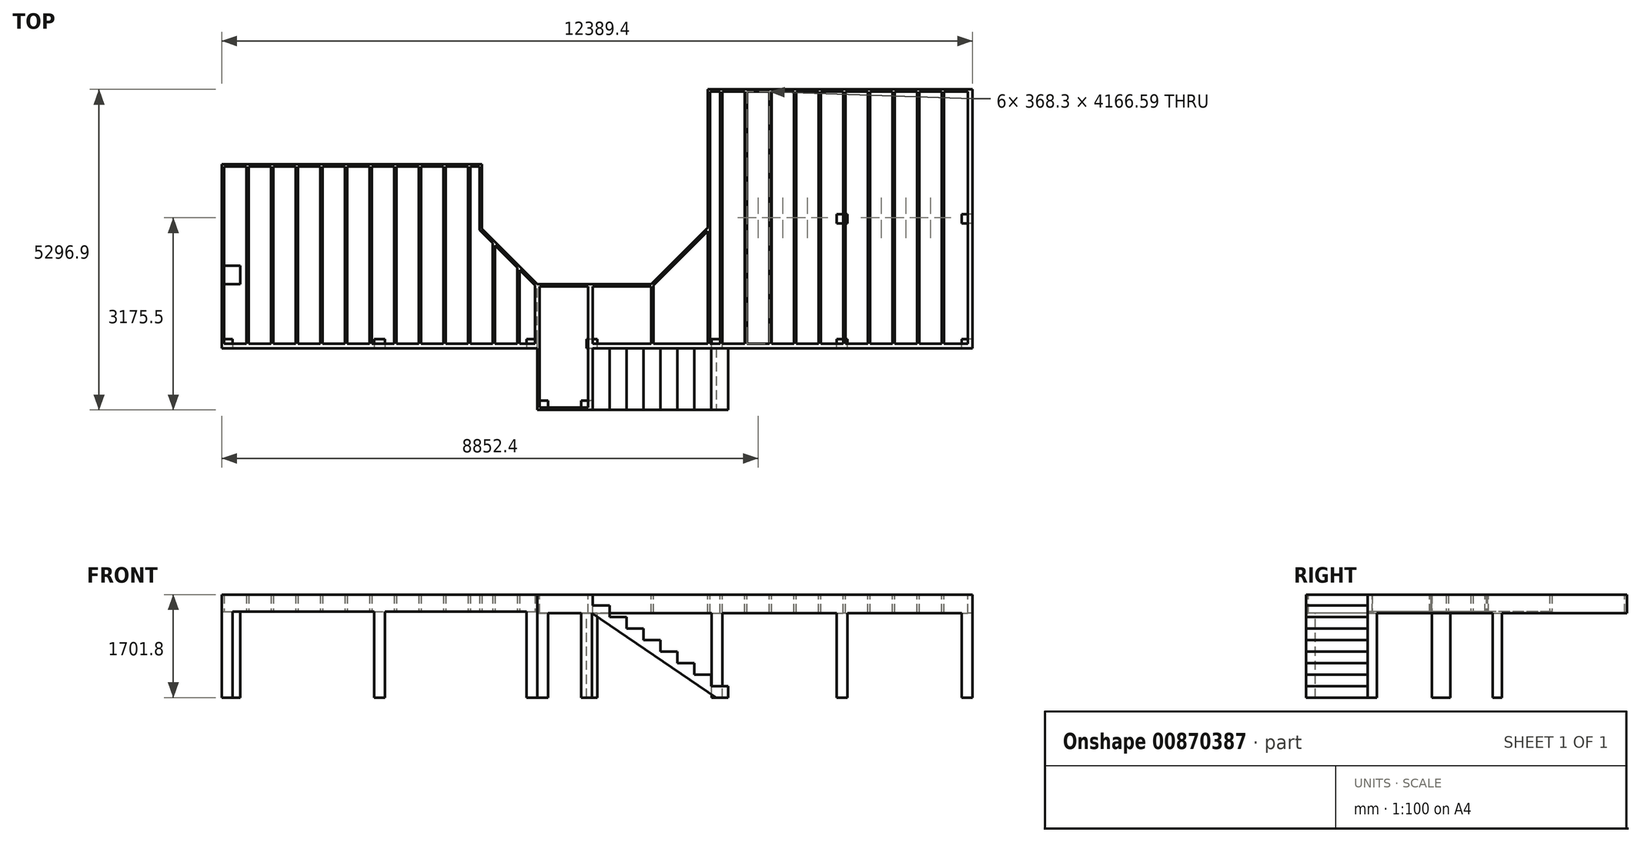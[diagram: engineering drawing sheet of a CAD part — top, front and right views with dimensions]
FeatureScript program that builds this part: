
annotation { "Feature Type Name" : "Feature", "Feature Type Description" : "" }
export const myFeature = defineFeature(function(context is Context, id is Id, definition is map)
    precondition{}
    {
        {
            var Q0;
            Q0=qCreatedBy(makeId("Top.planeOp"),FACE);
            var sketch = newSketch(context, id + "F0", { "sketchPlane" : qUnion([Q0])});
            skLineSegment(sketch, "E0.bottom", {"start": v(0, -1676.4) * mm, "end": v(304.8, -1676.4) * mm});
            skLineSegment(sketch, "E0.top", {"start": v(0, -1981.2) * mm, "end": v(304.8, -1981.2) * mm});
            skLineSegment(sketch, "E0.left", {"start": v(0, -1676.4) * mm, "end": v(0, -1981.2) * mm});
            skLineSegment(sketch, "E0.right", {"start": v(304.8, -1676.4) * mm, "end": v(304.8, -1981.2) * mm});
            skLineSegment(sketch, "E1.bottom", {"start": v(0, -2889.75) * mm, "end": v(177.8, -2889.75) * mm});
            skLineSegment(sketch, "E1.top", {"start": v(0, -3042.15) * mm, "end": v(177.8, -3042.15) * mm});
            skLineSegment(sketch, "E1.left", {"start": v(0, -2889.75) * mm, "end": v(0, -3042.15) * mm});
            skLineSegment(sketch, "E1.right", {"start": v(177.8, -2889.75) * mm, "end": v(177.8, -3042.15) * mm});
            skLineSegment(sketch, "E2.bottom", {"start": v(2514.6, -2889.75) * mm, "end": v(2692.4, -2889.75) * mm});
            skLineSegment(sketch, "E2.top", {"start": v(2514.6, -3042.15) * mm, "end": v(2692.4, -3042.15) * mm});
            skLineSegment(sketch, "E2.left", {"start": v(2514.6, -2889.75) * mm, "end": v(2514.6, -3042.15) * mm});
            skLineSegment(sketch, "E2.right", {"start": v(2692.4, -2889.75) * mm, "end": v(2692.4, -3042.15) * mm});
            skLineSegment(sketch, "E3.bottom", {"start": v(5029.2, -2889.75) * mm, "end": v(5207, -2889.75) * mm});
            skLineSegment(sketch, "E3.top", {"start": v(5029.2, -3042.15) * mm, "end": v(5207, -3042.15) * mm});
            skLineSegment(sketch, "E3.left", {"start": v(5029.2, -2889.75) * mm, "end": v(5029.2, -3042.15) * mm});
            skLineSegment(sketch, "E3.right", {"start": v(5207, -2889.75) * mm, "end": v(5207, -3042.15) * mm});
            skLineSegment(sketch, "E4", {"start": v(0, 0) * mm, "end": v(4292.6, 0) * mm, "construction": true});
            skLineSegment(sketch, "E5", {"start": v(4292.6, 0) * mm, "end": v(4292.6, -1066.8) * mm, "construction": true});
            skLineSegment(sketch, "E6", {"start": v(4292.6, -1066.8) * mm, "end": v(5226.55, -2000.75) * mm, "construction": true});
            skLineSegment(sketch, "E7", {"start": v(5226.55, -2000.75) * mm, "end": v(7106.15, -2000.75) * mm, "construction": true});
            skSolve(sketch);
        }
        {
            var Q0;
            Q0=qSketchRegion(id+"F0",true);
            extrude(context, id + "F1", {"entities" : qUnion([Q0]), "depth" : 1422.4 * mm, "offsetDistance" : 25.4 * mm});
        }
        {
            var Q0;
            Q0=makeQuery(id+"F1.opExtrude","CAP_FACE",FACE,{"disambiguationData":[OSD([sQuery(id+"F0.wireOp",EDGE,"E0.bottom"),sQuery(id+"F0.wireOp",EDGE,"E0.top"),sQuery(id+"F0.wireOp",EDGE,"E0.left"),sQuery(id+"F0.wireOp",EDGE,"E0.right")])],"isStart":false});
            var sketch = newSketch(context, id + "F2", { "sketchPlane" : qUnion([Q0])});
            skLineSegment(sketch, "E8.0", {"start": v(0, 0) * mm, "end": v(4292.6, 0) * mm});
            skLineSegment(sketch, "E9.0", {"start": v(4292.6, 0) * mm, "end": v(4292.6, -1066.8) * mm});
            skLineSegment(sketch, "E9.1", {"start": v(4292.6, -1066.8) * mm, "end": v(5207, -1981.2) * mm});
            skLineSegment(sketch, "E10", {"start": v(0, 0) * mm, "end": v(0, -3042.15) * mm});
            skLineSegment(sketch, "E11", {"start": v(0, -3042.15) * mm, "end": v(5207, -3042.15) * mm});
            skLineSegment(sketch, "E12", {"start": v(5207, -3042.15) * mm, "end": v(5207, -1981.2) * mm});
            skPoint(sketch, "E13.orphan", {"position": v(5226.55, -2000.75) * mm});
            skLineSegment(sketch, "E14.0", {"start": v(4254.5, -38.1) * mm, "end": v(4254.5, -1082.58) * mm});
            skLineSegment(sketch, "E14.1", {"start": v(5168.9, -3004.05) * mm, "end": v(5168.9, -1996.98) * mm});
            skLineSegment(sketch, "E14.2", {"start": v(38.1, -3004.05) * mm, "end": v(5168.9, -3004.05) * mm});
            skLineSegment(sketch, "E14.3", {"start": v(4254.5, -1082.58) * mm, "end": v(5168.9, -1996.98) * mm});
            skLineSegment(sketch, "E14.4", {"start": v(38.1, -38.1) * mm, "end": v(38.1, -3004.05) * mm});
            skLineSegment(sketch, "E14.5", {"start": v(38.1, -38.1) * mm, "end": v(4254.5, -38.1) * mm});
            skSolve(sketch);
        }
        {
            var Q0;
            Q0=qSketchRegion(id+"F2",true);
            extrude(context, id + "F3", {"entities" : qUnion([Q0]), "operationType" : NewBodyOperationType.ADD, "depth" : 279.4 * mm, "offsetDistance" : 25.4 * mm});
        }
        {
            var Q0;
            Q0=makeQuery(id+"F1.opExtrude","CAP_FACE",FACE,{"disambiguationData":[OSD([sQuery(id+"F0.wireOp",EDGE,"E1.bottom"),sQuery(id+"F0.wireOp",EDGE,"E1.top"),sQuery(id+"F0.wireOp",EDGE,"E1.left"),sQuery(id+"F0.wireOp",EDGE,"E1.right")])],"isStart":false});
            var sketch = newSketch(context, id + "F4", { "sketchPlane" : qUnion([Q0])});
            skPoint(sketch, "E15.oppositeSnap0", {"position": v(38.1, -2965.95) * mm});
            skLineSegment(sketch, "E15.bottom", {"start": v(38.1, -3004.05) * mm, "end": v(5168.9, -3004.05) * mm});
            skLineSegment(sketch, "E15.top", {"start": v(38.1, -2965.95) * mm, "end": v(5168.9, -2965.95) * mm});
            skLineSegment(sketch, "E15.left", {"start": v(38.1, -3004.05) * mm, "end": v(38.1, -2965.95) * mm});
            skLineSegment(sketch, "E15.right", {"start": v(5168.9, -3004.05) * mm, "end": v(5168.9, -2965.95) * mm});
            skSolve(sketch);
        }
        {
            var Q0;
            Q0=qSketchRegion(id+"F4",true);
            var Q1;
            Q1=makeQuery(id+"F3.opExtrude","CAP_FACE",FACE,{"disambiguationData":[OSD([sQuery(id+"F2.wireOp",EDGE,"E8.0"),sQuery(id+"F2.wireOp",EDGE,"E9.0"),sQuery(id+"F2.wireOp",EDGE,"E9.1"),sQuery(id+"F2.wireOp",EDGE,"E10"),sQuery(id+"F2.wireOp",EDGE,"E11"),sQuery(id+"F2.wireOp",EDGE,"E12"),sQuery(id+"F2.wireOp",EDGE,"E14.0"),sQuery(id+"F2.wireOp",EDGE,"E14.1"),sQuery(id+"F2.wireOp",EDGE,"E14.2"),sQuery(id+"F2.wireOp",EDGE,"E14.3"),sQuery(id+"F2.wireOp",EDGE,"E14.4"),sQuery(id+"F2.wireOp",EDGE,"E14.5")])],"isStart":false});
            extrude(context, id + "F5", {"entities" : qUnion([Q0]), "operationType" : NewBodyOperationType.ADD, "endBound" : BoundingType.UP_TO_SURFACE, "depth" : 25.4 * mm, "endBoundEntityFace" : qUnion([Q1]), "offsetDistance" : 25.4 * mm});
        }
        {
            var Q0;
            Q0=makeQuery(id+"F1.opExtrude","CAP_FACE",FACE,{"disambiguationData":[OSD([sQuery(id+"F0.wireOp",EDGE,"E0.bottom"),sQuery(id+"F0.wireOp",EDGE,"E0.top"),sQuery(id+"F0.wireOp",EDGE,"E0.left"),sQuery(id+"F0.wireOp",EDGE,"E0.right")])],"isStart":false});
            var sketch = newSketch(context, id + "F6", { "sketchPlane" : qUnion([Q0])});
            skLineSegment(sketch, "E16.bottom", {"start": v(406.4, -38.1) * mm, "end": v(444.5, -38.1) * mm});
            skLineSegment(sketch, "E16.top", {"start": v(406.4, -2965.95) * mm, "end": v(444.5, -2965.95) * mm});
            skLineSegment(sketch, "E16.left", {"start": v(406.4, -38.1) * mm, "end": v(406.4, -2965.95) * mm});
            skLineSegment(sketch, "E16.right", {"start": v(444.5, -38.1) * mm, "end": v(444.5, -2965.95) * mm});
            skLineSegment(sketch, "E17.1.0.0", {"start": v(850.9, -38.1) * mm, "end": v(850.9, -2965.95) * mm});
            skLineSegment(sketch, "E17.1.0.1", {"start": v(812.8, -38.1) * mm, "end": v(812.8, -2965.95) * mm});
            skLineSegment(sketch, "E17.1.0.2", {"start": v(812.8, -38.1) * mm, "end": v(850.9, -38.1) * mm});
            skLineSegment(sketch, "E17.1.0.3", {"start": v(812.8, -2965.95) * mm, "end": v(850.9, -2965.95) * mm});
            skLineSegment(sketch, "E17.2.0.0", {"start": v(1257.3, -38.1) * mm, "end": v(1257.3, -2965.95) * mm});
            skLineSegment(sketch, "E17.2.0.1", {"start": v(1219.2, -38.1) * mm, "end": v(1219.2, -2965.95) * mm});
            skLineSegment(sketch, "E17.2.0.2", {"start": v(1219.2, -38.1) * mm, "end": v(1257.3, -38.1) * mm});
            skLineSegment(sketch, "E17.2.0.3", {"start": v(1219.2, -2965.95) * mm, "end": v(1257.3, -2965.95) * mm});
            skLineSegment(sketch, "E17.3.0.0", {"start": v(1663.7, -38.1) * mm, "end": v(1663.7, -2965.95) * mm});
            skLineSegment(sketch, "E17.3.0.1", {"start": v(1625.6, -38.1) * mm, "end": v(1625.6, -2965.95) * mm});
            skLineSegment(sketch, "E17.3.0.2", {"start": v(1625.6, -38.1) * mm, "end": v(1663.7, -38.1) * mm});
            skLineSegment(sketch, "E17.3.0.3", {"start": v(1625.6, -2965.95) * mm, "end": v(1663.7, -2965.95) * mm});
            skLineSegment(sketch, "E17.4.0.0", {"start": v(2070.1, -38.1) * mm, "end": v(2070.1, -2965.95) * mm});
            skLineSegment(sketch, "E17.4.0.1", {"start": v(2032, -38.1) * mm, "end": v(2032, -2965.95) * mm});
            skLineSegment(sketch, "E17.4.0.2", {"start": v(2032, -38.1) * mm, "end": v(2070.1, -38.1) * mm});
            skLineSegment(sketch, "E17.4.0.3", {"start": v(2032, -2965.95) * mm, "end": v(2070.1, -2965.95) * mm});
            skLineSegment(sketch, "E17.5.0.0", {"start": v(2476.5, -38.1) * mm, "end": v(2476.5, -2965.95) * mm});
            skLineSegment(sketch, "E17.5.0.1", {"start": v(2438.4, -38.1) * mm, "end": v(2438.4, -2965.95) * mm});
            skLineSegment(sketch, "E17.5.0.2", {"start": v(2438.4, -38.1) * mm, "end": v(2476.5, -38.1) * mm});
            skLineSegment(sketch, "E17.5.0.3", {"start": v(2438.4, -2965.95) * mm, "end": v(2476.5, -2965.95) * mm});
            skLineSegment(sketch, "E17.6.0.0", {"start": v(2882.9, -38.1) * mm, "end": v(2882.9, -2965.95) * mm});
            skLineSegment(sketch, "E17.6.0.1", {"start": v(2844.8, -38.1) * mm, "end": v(2844.8, -2965.95) * mm});
            skLineSegment(sketch, "E17.6.0.2", {"start": v(2844.8, -38.1) * mm, "end": v(2882.9, -38.1) * mm});
            skLineSegment(sketch, "E17.6.0.3", {"start": v(2844.8, -2965.95) * mm, "end": v(2882.9, -2965.95) * mm});
            skLineSegment(sketch, "E17.7.0.0", {"start": v(3289.3, -38.1) * mm, "end": v(3289.3, -2965.95) * mm});
            skLineSegment(sketch, "E17.7.0.1", {"start": v(3251.2, -38.1) * mm, "end": v(3251.2, -2965.95) * mm});
            skLineSegment(sketch, "E17.7.0.2", {"start": v(3251.2, -38.1) * mm, "end": v(3289.3, -38.1) * mm});
            skLineSegment(sketch, "E17.7.0.3", {"start": v(3251.2, -2965.95) * mm, "end": v(3289.3, -2965.95) * mm});
            skLineSegment(sketch, "E17.8.0.0", {"start": v(3695.7, -38.1) * mm, "end": v(3695.7, -2965.95) * mm});
            skLineSegment(sketch, "E17.8.0.1", {"start": v(3657.6, -38.1) * mm, "end": v(3657.6, -2965.95) * mm});
            skLineSegment(sketch, "E17.8.0.2", {"start": v(3657.6, -38.1) * mm, "end": v(3695.7, -38.1) * mm});
            skLineSegment(sketch, "E17.8.0.3", {"start": v(3657.6, -2965.95) * mm, "end": v(3695.7, -2965.95) * mm});
            skLineSegment(sketch, "E17.9.0.0", {"start": v(4102.1, -38.1) * mm, "end": v(4102.1, -2965.95) * mm});
            skLineSegment(sketch, "E17.9.0.1", {"start": v(4064, -38.1) * mm, "end": v(4064, -2965.95) * mm});
            skLineSegment(sketch, "E17.9.0.2", {"start": v(4064, -38.1) * mm, "end": v(4102.1, -38.1) * mm});
            skLineSegment(sketch, "E17.9.0.3", {"start": v(4064, -2965.95) * mm, "end": v(4102.1, -2965.95) * mm});
            skLineSegment(sketch, "E17.direction1", {"start": v(406.4, -2965.95) * mm, "end": v(812.8, -2965.95) * mm, "construction": true});
            skLineSegment(sketch, "E18.top", {"start": v(4470.4, -2965.95) * mm, "end": v(4508.5, -2965.95) * mm});
            skLineSegment(sketch, "E18.left", {"start": v(4470.4, -1298.48) * mm, "end": v(4470.4, -2965.95) * mm});
            skLineSegment(sketch, "E18.right", {"start": v(4508.5, -1336.58) * mm, "end": v(4508.5, -2965.95) * mm});
            skLineSegment(sketch, "E19.top", {"start": v(4876.8, -2965.95) * mm, "end": v(4914.9, -2965.95) * mm});
            skLineSegment(sketch, "E19.left", {"start": v(4876.8, -1704.88) * mm, "end": v(4876.8, -2965.95) * mm});
            skLineSegment(sketch, "E19.right", {"start": v(4914.9, -1742.98) * mm, "end": v(4914.9, -2965.95) * mm});
            skLineSegment(sketch, "E20", {"start": v(4470.4, -1298.48) * mm, "end": v(4508.5, -1336.58) * mm});
            skLineSegment(sketch, "E21.trimOffspring", {"start": v(4876.8, -1704.88) * mm, "end": v(4914.9, -1742.98) * mm});
            skSolve(sketch);
        }
        {
            var Q0;
            Q0=qSketchRegion(id+"F6",true);
            var Q1;
            {var subQ0=sQuery(id+"F2.wireOp",EDGE,"E14.5");var subQ1=sQuery(id+"F2.wireOp",EDGE,"E14.4");var subQ2=sQuery(id+"F2.wireOp",EDGE,"E14.3");var subQ3=sQuery(id+"F2.wireOp",EDGE,"E14.2");var subQ4=sQuery(id+"F2.wireOp",EDGE,"E14.1");var subQ5=sQuery(id+"F2.wireOp",EDGE,"E14.0");var subQ6=sQuery(id+"F2.wireOp",EDGE,"E12");var subQ7=sQuery(id+"F2.wireOp",EDGE,"E11");var subQ8=sQuery(id+"F2.wireOp",EDGE,"E10");var subQ9=sQuery(id+"F2.wireOp",EDGE,"E9.1");var subQ10=sQuery(id+"F2.wireOp",EDGE,"E9.0");var subQ11=sQuery(id+"F2.wireOp",EDGE,"E8.0");Q1=makeQuery(id+"F5.boolean.opBoolean","MERGE",FACE,{"derivedFrom":[makeQuery(id+"F3.opExtrude","CAP_FACE",FACE,{"disambiguationData":[OSD([subQ11,subQ10,subQ9,subQ8,subQ7,subQ6,subQ5,subQ4,subQ3,subQ2,subQ1,subQ0])],"isStart":false}),makeQuery(id+"F5.opExtrude","CAP_FACE",FACE,{"disambiguationData":[OSD([subQ11,subQ10,subQ9,subQ8,subQ7,subQ6,subQ5,subQ4,subQ3,subQ2,subQ1,subQ0])],"isStart":false})]});}
            extrude(context, id + "F7", {"entities" : qUnion([Q0]), "operationType" : NewBodyOperationType.ADD, "endBound" : BoundingType.UP_TO_SURFACE, "depth" : 25.4 * mm, "endBoundEntityFace" : qUnion([Q1]), "offsetDistance" : 25.4 * mm});
        }
        {
            var Q0;
            Q0=makeQuery(id+"F7.boolean.opBoolean","MERGE",FACE,{"derivedFrom":[makeQuery(id+"F5.boolean.opBoolean","MERGE",FACE,{"derivedFrom":[makeQuery(id+"F3.opExtrude","CAP_FACE",FACE,{"disambiguationData":[OSD([sQuery(id+"F2.wireOp",EDGE,"E8.0"),sQuery(id+"F2.wireOp",EDGE,"E9.0"),sQuery(id+"F2.wireOp",EDGE,"E9.1"),sQuery(id+"F2.wireOp",EDGE,"E10"),sQuery(id+"F2.wireOp",EDGE,"E11"),sQuery(id+"F2.wireOp",EDGE,"E12"),sQuery(id+"F2.wireOp",EDGE,"E14.0"),sQuery(id+"F2.wireOp",EDGE,"E14.1"),sQuery(id+"F2.wireOp",EDGE,"E14.2"),sQuery(id+"F2.wireOp",EDGE,"E14.3"),sQuery(id+"F2.wireOp",EDGE,"E14.4"),sQuery(id+"F2.wireOp",EDGE,"E14.5")])],"isStart":false}),makeQuery(id+"F5.opExtrude","CAP_FACE",FACE,{"disambiguationData":[OSD([sQuery(id+"F4.wireOp",EDGE,"E15.bottom"),sQuery(id+"F4.wireOp",EDGE,"E15.top"),sQuery(id+"F4.wireOp",EDGE,"E15.left"),sQuery(id+"F4.wireOp",EDGE,"E15.right")])],"isStart":false})]}),makeQuery(id+"F7.opExtrude","CAP_FACE",FACE,{"disambiguationData":[OSD([sQuery(id+"F6.wireOp",EDGE,"E16.bottom"),sQuery(id+"F6.wireOp",EDGE,"E16.top"),sQuery(id+"F6.wireOp",EDGE,"E16.left"),sQuery(id+"F6.wireOp",EDGE,"E16.right")])],"isStart":false}),makeQuery(id+"F7.opExtrude","CAP_FACE",FACE,{"disambiguationData":[OSD([sQuery(id+"F6.wireOp",EDGE,"E17.1.0.0"),sQuery(id+"F6.wireOp",EDGE,"E17.1.0.1"),sQuery(id+"F6.wireOp",EDGE,"E17.1.0.2"),sQuery(id+"F6.wireOp",EDGE,"E17.1.0.3")])],"isStart":false}),makeQuery(id+"F7.opExtrude","CAP_FACE",FACE,{"disambiguationData":[OSD([sQuery(id+"F6.wireOp",EDGE,"E17.2.0.0"),sQuery(id+"F6.wireOp",EDGE,"E17.2.0.1"),sQuery(id+"F6.wireOp",EDGE,"E17.2.0.2"),sQuery(id+"F6.wireOp",EDGE,"E17.2.0.3")])],"isStart":false}),makeQuery(id+"F7.opExtrude","CAP_FACE",FACE,{"disambiguationData":[OSD([sQuery(id+"F6.wireOp",EDGE,"E17.3.0.0"),sQuery(id+"F6.wireOp",EDGE,"E17.3.0.1"),sQuery(id+"F6.wireOp",EDGE,"E17.3.0.2"),sQuery(id+"F6.wireOp",EDGE,"E17.3.0.3")])],"isStart":false}),makeQuery(id+"F7.opExtrude","CAP_FACE",FACE,{"disambiguationData":[OSD([sQuery(id+"F6.wireOp",EDGE,"E17.4.0.0"),sQuery(id+"F6.wireOp",EDGE,"E17.4.0.1"),sQuery(id+"F6.wireOp",EDGE,"E17.4.0.2"),sQuery(id+"F6.wireOp",EDGE,"E17.4.0.3")])],"isStart":false}),makeQuery(id+"F7.opExtrude","CAP_FACE",FACE,{"disambiguationData":[OSD([sQuery(id+"F6.wireOp",EDGE,"E17.5.0.0"),sQuery(id+"F6.wireOp",EDGE,"E17.5.0.1"),sQuery(id+"F6.wireOp",EDGE,"E17.5.0.2"),sQuery(id+"F6.wireOp",EDGE,"E17.5.0.3")])],"isStart":false}),makeQuery(id+"F7.opExtrude","CAP_FACE",FACE,{"disambiguationData":[OSD([sQuery(id+"F6.wireOp",EDGE,"E17.6.0.0"),sQuery(id+"F6.wireOp",EDGE,"E17.6.0.1"),sQuery(id+"F6.wireOp",EDGE,"E17.6.0.2"),sQuery(id+"F6.wireOp",EDGE,"E17.6.0.3")])],"isStart":false}),makeQuery(id+"F7.opExtrude","CAP_FACE",FACE,{"disambiguationData":[OSD([sQuery(id+"F6.wireOp",EDGE,"E17.7.0.0"),sQuery(id+"F6.wireOp",EDGE,"E17.7.0.1"),sQuery(id+"F6.wireOp",EDGE,"E17.7.0.2"),sQuery(id+"F6.wireOp",EDGE,"E17.7.0.3")])],"isStart":false}),makeQuery(id+"F7.opExtrude","CAP_FACE",FACE,{"disambiguationData":[OSD([sQuery(id+"F6.wireOp",EDGE,"E17.8.0.0"),sQuery(id+"F6.wireOp",EDGE,"E17.8.0.1"),sQuery(id+"F6.wireOp",EDGE,"E17.8.0.2"),sQuery(id+"F6.wireOp",EDGE,"E17.8.0.3")])],"isStart":false}),makeQuery(id+"F7.opExtrude","CAP_FACE",FACE,{"disambiguationData":[OSD([sQuery(id+"F6.wireOp",EDGE,"E17.9.0.0"),sQuery(id+"F6.wireOp",EDGE,"E17.9.0.1"),sQuery(id+"F6.wireOp",EDGE,"E17.9.0.2"),sQuery(id+"F6.wireOp",EDGE,"E17.9.0.3")])],"isStart":false}),makeQuery(id+"F7.opExtrude","CAP_FACE",FACE,{"disambiguationData":[OSD([sQuery(id+"F6.wireOp",EDGE,"E18.top"),sQuery(id+"F6.wireOp",EDGE,"E18.left"),sQuery(id+"F6.wireOp",EDGE,"E18.right"),sQuery(id+"F6.wireOp",EDGE,"E20")])],"isStart":false}),makeQuery(id+"F7.opExtrude","CAP_FACE",FACE,{"disambiguationData":[OSD([sQuery(id+"F6.wireOp",EDGE,"E19.top"),sQuery(id+"F6.wireOp",EDGE,"E19.left"),sQuery(id+"F6.wireOp",EDGE,"E19.right"),sQuery(id+"F6.wireOp",EDGE,"E21.trimOffspring")])],"isStart":false})]});
            var sketch = newSketch(context, id + "F8", { "sketchPlane" : qUnion([Q0])});
            skLineSegment(sketch, "E22", {"start": v(5207, -1981.2) * mm, "end": v(5207, -3042.15) * mm});
            skLineSegment(sketch, "E23", {"start": v(5207, -1981.2) * mm, "end": v(7086.6, -1981.2) * mm});
            skLineSegment(sketch, "E24", {"start": v(7086.6, -1981.2) * mm, "end": v(8020.55, -1047.25) * mm});
            skLineSegment(sketch, "E25", {"start": v(8020.55, -1047.25) * mm, "end": v(8020.55, 1238.75) * mm});
            skLineSegment(sketch, "E26", {"start": v(8020.55, 1238.75) * mm, "end": v(12389.35, 1238.75) * mm});
            skLineSegment(sketch, "E27", {"start": v(12389.35, 1238.75) * mm, "end": v(12389.35, -3042.15) * mm});
            skLineSegment(sketch, "E28", {"start": v(5207, -3042.15) * mm, "end": v(12389.35, -3042.15) * mm});
            skSolve(sketch);
        }
        {
            var Q0;
            Q0=qSketchRegion(id+"F8",true);
            extrude(context, id + "F9", {"entities" : qUnion([Q0]), "operationType" : NewBodyOperationType.ADD, "oppositeDirection" : true, "depth" : 304.8 * mm, "offsetDistance" : 25.4 * mm});
        }
        {
            var Q0;
            Q0=makeQuery(id+"F9.boolean.opBoolean","MERGE",FACE,{"derivedFrom":[makeQuery(id+"F7.boolean.opBoolean","MERGE",FACE,{"derivedFrom":[makeQuery(id+"F5.boolean.opBoolean","MERGE",FACE,{"derivedFrom":[makeQuery(id+"F3.opExtrude","CAP_FACE",FACE,{"disambiguationData":[OSD([sQuery(id+"F2.wireOp",EDGE,"E8.0"),sQuery(id+"F2.wireOp",EDGE,"E9.0"),sQuery(id+"F2.wireOp",EDGE,"E9.1"),sQuery(id+"F2.wireOp",EDGE,"E10"),sQuery(id+"F2.wireOp",EDGE,"E11"),sQuery(id+"F2.wireOp",EDGE,"E12"),sQuery(id+"F2.wireOp",EDGE,"E14.0"),sQuery(id+"F2.wireOp",EDGE,"E14.1"),sQuery(id+"F2.wireOp",EDGE,"E14.2"),sQuery(id+"F2.wireOp",EDGE,"E14.3"),sQuery(id+"F2.wireOp",EDGE,"E14.4"),sQuery(id+"F2.wireOp",EDGE,"E14.5")])],"isStart":false}),makeQuery(id+"F5.opExtrude","CAP_FACE",FACE,{"disambiguationData":[OSD([sQuery(id+"F4.wireOp",EDGE,"E15.bottom"),sQuery(id+"F4.wireOp",EDGE,"E15.top"),sQuery(id+"F4.wireOp",EDGE,"E15.left"),sQuery(id+"F4.wireOp",EDGE,"E15.right")])],"isStart":false})]}),makeQuery(id+"F7.opExtrude","CAP_FACE",FACE,{"disambiguationData":[OSD([sQuery(id+"F6.wireOp",EDGE,"E16.bottom"),sQuery(id+"F6.wireOp",EDGE,"E16.top"),sQuery(id+"F6.wireOp",EDGE,"E16.left"),sQuery(id+"F6.wireOp",EDGE,"E16.right")])],"isStart":false}),makeQuery(id+"F7.opExtrude","CAP_FACE",FACE,{"disambiguationData":[OSD([sQuery(id+"F6.wireOp",EDGE,"E17.1.0.0"),sQuery(id+"F6.wireOp",EDGE,"E17.1.0.1"),sQuery(id+"F6.wireOp",EDGE,"E17.1.0.2"),sQuery(id+"F6.wireOp",EDGE,"E17.1.0.3")])],"isStart":false}),makeQuery(id+"F7.opExtrude","CAP_FACE",FACE,{"disambiguationData":[OSD([sQuery(id+"F6.wireOp",EDGE,"E17.2.0.0"),sQuery(id+"F6.wireOp",EDGE,"E17.2.0.1"),sQuery(id+"F6.wireOp",EDGE,"E17.2.0.2"),sQuery(id+"F6.wireOp",EDGE,"E17.2.0.3")])],"isStart":false}),makeQuery(id+"F7.opExtrude","CAP_FACE",FACE,{"disambiguationData":[OSD([sQuery(id+"F6.wireOp",EDGE,"E17.3.0.0"),sQuery(id+"F6.wireOp",EDGE,"E17.3.0.1"),sQuery(id+"F6.wireOp",EDGE,"E17.3.0.2"),sQuery(id+"F6.wireOp",EDGE,"E17.3.0.3")])],"isStart":false}),makeQuery(id+"F7.opExtrude","CAP_FACE",FACE,{"disambiguationData":[OSD([sQuery(id+"F6.wireOp",EDGE,"E17.4.0.0"),sQuery(id+"F6.wireOp",EDGE,"E17.4.0.1"),sQuery(id+"F6.wireOp",EDGE,"E17.4.0.2"),sQuery(id+"F6.wireOp",EDGE,"E17.4.0.3")])],"isStart":false}),makeQuery(id+"F7.opExtrude","CAP_FACE",FACE,{"disambiguationData":[OSD([sQuery(id+"F6.wireOp",EDGE,"E17.5.0.0"),sQuery(id+"F6.wireOp",EDGE,"E17.5.0.1"),sQuery(id+"F6.wireOp",EDGE,"E17.5.0.2"),sQuery(id+"F6.wireOp",EDGE,"E17.5.0.3")])],"isStart":false}),makeQuery(id+"F7.opExtrude","CAP_FACE",FACE,{"disambiguationData":[OSD([sQuery(id+"F6.wireOp",EDGE,"E17.6.0.0"),sQuery(id+"F6.wireOp",EDGE,"E17.6.0.1"),sQuery(id+"F6.wireOp",EDGE,"E17.6.0.2"),sQuery(id+"F6.wireOp",EDGE,"E17.6.0.3")])],"isStart":false}),makeQuery(id+"F7.opExtrude","CAP_FACE",FACE,{"disambiguationData":[OSD([sQuery(id+"F6.wireOp",EDGE,"E17.7.0.0"),sQuery(id+"F6.wireOp",EDGE,"E17.7.0.1"),sQuery(id+"F6.wireOp",EDGE,"E17.7.0.2"),sQuery(id+"F6.wireOp",EDGE,"E17.7.0.3")])],"isStart":false}),makeQuery(id+"F7.opExtrude","CAP_FACE",FACE,{"disambiguationData":[OSD([sQuery(id+"F6.wireOp",EDGE,"E17.8.0.0"),sQuery(id+"F6.wireOp",EDGE,"E17.8.0.1"),sQuery(id+"F6.wireOp",EDGE,"E17.8.0.2"),sQuery(id+"F6.wireOp",EDGE,"E17.8.0.3")])],"isStart":false}),makeQuery(id+"F7.opExtrude","CAP_FACE",FACE,{"disambiguationData":[OSD([sQuery(id+"F6.wireOp",EDGE,"E17.9.0.0"),sQuery(id+"F6.wireOp",EDGE,"E17.9.0.1"),sQuery(id+"F6.wireOp",EDGE,"E17.9.0.2"),sQuery(id+"F6.wireOp",EDGE,"E17.9.0.3")])],"isStart":false}),makeQuery(id+"F7.opExtrude","CAP_FACE",FACE,{"disambiguationData":[OSD([sQuery(id+"F6.wireOp",EDGE,"E18.top"),sQuery(id+"F6.wireOp",EDGE,"E18.left"),sQuery(id+"F6.wireOp",EDGE,"E18.right"),sQuery(id+"F6.wireOp",EDGE,"E20")])],"isStart":false}),makeQuery(id+"F7.opExtrude","CAP_FACE",FACE,{"disambiguationData":[OSD([sQuery(id+"F6.wireOp",EDGE,"E19.top"),sQuery(id+"F6.wireOp",EDGE,"E19.left"),sQuery(id+"F6.wireOp",EDGE,"E19.right"),sQuery(id+"F6.wireOp",EDGE,"E21.trimOffspring")])],"isStart":false})]}),makeQuery(id+"F9.opExtrude","CAP_FACE",FACE,{"disambiguationData":[OSD([sQuery(id+"F8.wireOp",EDGE,"E22"),sQuery(id+"F8.wireOp",EDGE,"E23"),sQuery(id+"F8.wireOp",EDGE,"E24"),sQuery(id+"F8.wireOp",EDGE,"E25"),sQuery(id+"F8.wireOp",EDGE,"E26"),sQuery(id+"F8.wireOp",EDGE,"E27"),sQuery(id+"F8.wireOp",EDGE,"E28")])],"isStart":true})]});
            var sketch = newSketch(context, id + "F10", { "sketchPlane" : qUnion([Q0])});
            skLineSegment(sketch, "E29.bottom", {"start": v(6121.4, -3042.15) * mm, "end": v(5207, -3042.15) * mm});
            skLineSegment(sketch, "E29.top", {"start": v(6121.4, -4058.15) * mm, "end": v(5207, -4058.15) * mm});
            skLineSegment(sketch, "E29.left", {"start": v(6121.4, -3042.15) * mm, "end": v(6121.4, -4058.15) * mm});
            skLineSegment(sketch, "E29.right", {"start": v(5207, -3042.15) * mm, "end": v(5207, -4058.15) * mm});
            skSolve(sketch);
        }
        {
            var Q0;
            Q0=qSketchRegion(id+"F10",true);
            var Q1;
            Q1=makeQuery(id+"F9.opExtrude","CAP_FACE",FACE,{"disambiguationData":[OSD([sQuery(id+"F8.wireOp",EDGE,"E22"),sQuery(id+"F8.wireOp",EDGE,"E23"),sQuery(id+"F8.wireOp",EDGE,"E24"),sQuery(id+"F8.wireOp",EDGE,"E25"),sQuery(id+"F8.wireOp",EDGE,"E26"),sQuery(id+"F8.wireOp",EDGE,"E27"),sQuery(id+"F8.wireOp",EDGE,"E28")])],"isStart":false});
            extrude(context, id + "F11", {"entities" : qUnion([Q0]), "operationType" : NewBodyOperationType.ADD, "endBound" : BoundingType.UP_TO_SURFACE, "oppositeDirection" : true, "depth" : 25.4 * mm, "endBoundEntityFace" : qUnion([Q1]), "offsetDistance" : 25.4 * mm});
        }
        {
            var Q0;
            Q0=makeQuery(id+"F11.opExtrude","SWEPT_FACE",FACE,{"disambiguationData":[OSD([sQuery(id+"F10.wireOp",EDGE,"E29.top")])]});
            var sketch = newSketch(context, id + "F12", { "sketchPlane" : qUnion([Q0])});
            skLineSegment(sketch, "E30", {"start": v(6121.4, 1701.8) * mm, "end": v(6121.4, 1524) * mm});
            skLineSegment(sketch, "E31", {"start": v(6121.4, 1524) * mm, "end": v(6400.8, 1524) * mm});
            skLineSegment(sketch, "E32", {"start": v(6400.8, 1524) * mm, "end": v(6400.8, 1333.5) * mm});
            skLineSegment(sketch, "E33", {"start": v(6400.8, 1333.5) * mm, "end": v(6680.2, 1333.5) * mm});
            skLineSegment(sketch, "E34", {"start": v(6680.2, 1333.5) * mm, "end": v(6680.2, 1143) * mm});
            skLineSegment(sketch, "E35", {"start": v(6680.2, 1143) * mm, "end": v(6959.6, 1143) * mm});
            skLineSegment(sketch, "E36", {"start": v(6959.6, 1143) * mm, "end": v(6959.6, 952.5) * mm});
            skLineSegment(sketch, "E37", {"start": v(6959.6, 952.5) * mm, "end": v(7239, 952.5) * mm});
            skLineSegment(sketch, "E38", {"start": v(7239, 952.5) * mm, "end": v(7239, 762) * mm});
            skLineSegment(sketch, "E39", {"start": v(7239, 762) * mm, "end": v(7518.4, 762) * mm});
            skLineSegment(sketch, "E40", {"start": v(7518.4, 762) * mm, "end": v(7518.4, 571.5) * mm});
            skLineSegment(sketch, "E41", {"start": v(7518.4, 571.5) * mm, "end": v(7797.8, 571.5) * mm});
            skLineSegment(sketch, "E42", {"start": v(7797.8, 571.5) * mm, "end": v(7797.8, 381) * mm});
            skLineSegment(sketch, "E43", {"start": v(7797.8, 381) * mm, "end": v(8077.2, 381) * mm});
            skLineSegment(sketch, "E44", {"start": v(8077.2, 381) * mm, "end": v(8077.2, 190.5) * mm});
            skLineSegment(sketch, "E45", {"start": v(8077.2, 190.5) * mm, "end": v(8356.6, 190.5) * mm});
            skLineSegment(sketch, "E46", {"start": v(8356.6, 190.5) * mm, "end": v(8356.6, 0) * mm});
            skLineSegment(sketch, "E47", {"start": v(6121.4, 1701.8) * mm, "end": v(5664.2, 1701.8) * mm});
            skLineSegment(sketch, "E48", {"start": v(5664.2, 1701.8) * mm, "end": v(8160.17, 0) * mm});
            skLineSegment(sketch, "E49", {"start": v(8160.17, 0) * mm, "end": v(8356.6, 0) * mm});
            skLineSegment(sketch, "E50", {"start": v(6680.2, 1333.5) * mm, "end": v(8077.2, 381) * mm, "construction": true});
            skSolve(sketch);
        }
        {
            var Q0;
            {var subQ0=sQuery(id+"F12.wireOp",EDGE,"E31");Q0=makeQuery(id+"F12.imprint","IMPRINT",FACE,{"disambiguationData":[TD([[makeQuery(id+"F12.imprint","IMPRINT",EDGE,{"derivedFrom":subQ0}),-1.0]])]});}
            var Q1;
            {var subQ0=sQuery(id+"F8.wireOp",EDGE,"E28");var subQ1=sQuery(id+"F8.wireOp",EDGE,"E27");var subQ7=sQuery(id+"F2.wireOp",EDGE,"E11");Q1=makeQuery(id+"F11.boolean.opBoolean","SPLIT",FACE,{"disambiguationData":[TD([makeQuery(id+"F9.opExtrude","SWEPT_FACE",FACE,{"disambiguationData":[OSD([subQ1])]})])],"derivedFrom":makeQuery(id+"F9.boolean.opBoolean","MERGE",FACE,{"derivedFrom":[makeQuery(id+"F3.boolean.opBoolean","MERGE",FACE,{"derivedFrom":[makeQuery(id+"F1.opExtrude","SWEPT_FACE",FACE,{"disambiguationData":[OSD([sQuery(id+"F0.wireOp",EDGE,"E1.top")])]}),makeQuery(id+"F1.opExtrude","SWEPT_FACE",FACE,{"disambiguationData":[OSD([sQuery(id+"F0.wireOp",EDGE,"E2.top")])]}),makeQuery(id+"F1.opExtrude","SWEPT_FACE",FACE,{"disambiguationData":[OSD([sQuery(id+"F0.wireOp",EDGE,"E3.top")])]}),makeQuery(id+"F3.opExtrude","SWEPT_FACE",FACE,{"disambiguationData":[OSD([subQ7])]})]}),makeQuery(id+"F9.opExtrude","SWEPT_FACE",FACE,{"disambiguationData":[OSD([subQ0])]})]})});}
            extrude(context, id + "F13", {"entities" : qUnion([Q0]), "operationType" : NewBodyOperationType.ADD, "endBound" : BoundingType.UP_TO_SURFACE, "oppositeDirection" : true, "depth" : 25.4 * mm, "endBoundEntityFace" : qUnion([Q1]), "offsetDistance" : 25.4 * mm});
        }
        {
            var Q0;
            Q0=makeQuery(id+"F11.boolean.opBoolean","MERGE",FACE,{"derivedFrom":[makeQuery(id+"F9.opExtrude","CAP_FACE",FACE,{"disambiguationData":[OSD([sQuery(id+"F8.wireOp",EDGE,"E22"),sQuery(id+"F8.wireOp",EDGE,"E23"),sQuery(id+"F8.wireOp",EDGE,"E24"),sQuery(id+"F8.wireOp",EDGE,"E25"),sQuery(id+"F8.wireOp",EDGE,"E26"),sQuery(id+"F8.wireOp",EDGE,"E27"),sQuery(id+"F8.wireOp",EDGE,"E28")])],"isStart":false}),makeQuery(id+"F11.opExtrude","CAP_FACE",FACE,{"disambiguationData":[OSD([sQuery(id+"F10.wireOp",EDGE,"E29.bottom"),sQuery(id+"F10.wireOp",EDGE,"E29.top"),sQuery(id+"F10.wireOp",EDGE,"E29.left"),sQuery(id+"F10.wireOp",EDGE,"E29.right")])],"isStart":false})]});
            var sketch = newSketch(context, id + "F14", { "sketchPlane" : qUnion([Q0])});
            skLineSegment(sketch, "E51.bottom", {"start": v(5384.8, 3905.75) * mm, "end": v(5207, 3905.75) * mm});
            skLineSegment(sketch, "E51.top", {"start": v(5384.8, 4058.15) * mm, "end": v(5207, 4058.15) * mm});
            skLineSegment(sketch, "E51.left", {"start": v(5384.8, 3905.75) * mm, "end": v(5384.8, 4058.15) * mm});
            skLineSegment(sketch, "E51.right", {"start": v(5207, 3905.75) * mm, "end": v(5207, 4058.15) * mm});
            skLineSegment(sketch, "E52.bottom", {"start": v(6111.24, 4058.15) * mm, "end": v(5933.44, 4058.15) * mm});
            skLineSegment(sketch, "E52.top", {"start": v(6111.24, 3905.75) * mm, "end": v(5933.44, 3905.75) * mm});
            skLineSegment(sketch, "E52.left", {"start": v(6111.24, 4058.15) * mm, "end": v(6111.24, 3905.75) * mm});
            skLineSegment(sketch, "E52.right", {"start": v(5933.44, 4058.15) * mm, "end": v(5933.44, 3905.75) * mm});
            skLineSegment(sketch, "E53.bottom", {"start": v(6200.14, 3042.15) * mm, "end": v(6022.34, 3042.15) * mm});
            skLineSegment(sketch, "E53.top", {"start": v(6200.14, 2889.75) * mm, "end": v(6022.34, 2889.75) * mm});
            skLineSegment(sketch, "E53.left", {"start": v(6200.14, 3042.15) * mm, "end": v(6200.14, 2889.75) * mm});
            skLineSegment(sketch, "E53.right", {"start": v(6022.34, 3042.15) * mm, "end": v(6022.34, 2889.75) * mm});
            skLineSegment(sketch, "E54.bottom", {"start": v(10326.28, 3042.15) * mm, "end": v(10148.48, 3042.15) * mm});
            skLineSegment(sketch, "E54.left", {"start": v(10326.28, 3042.15) * mm, "end": v(10326.28, 2889.75) * mm});
            skLineSegment(sketch, "E54.right", {"start": v(10148.48, 3042.15) * mm, "end": v(10148.48, 2889.75) * mm});
            skLineSegment(sketch, "E55.bottom", {"start": v(12389.35, 3042.15) * mm, "end": v(12211.55, 3042.15) * mm});
            skLineSegment(sketch, "E55.top", {"start": v(12389.35, 2889.75) * mm, "end": v(12211.55, 2889.75) * mm});
            skLineSegment(sketch, "E55.left", {"start": v(12389.35, 3042.15) * mm, "end": v(12389.35, 2889.75) * mm});
            skLineSegment(sketch, "E55.right", {"start": v(12211.55, 3042.15) * mm, "end": v(12211.55, 2889.75) * mm});
            skLineSegment(sketch, "E56.bottom", {"start": v(8085.4, 3042.15) * mm, "end": v(8263.2, 3042.15) * mm});
            skLineSegment(sketch, "E56.top", {"start": v(8085.4, 2889.75) * mm, "end": v(8263.2, 2889.75) * mm});
            skLineSegment(sketch, "E56.left", {"start": v(8085.4, 3042.15) * mm, "end": v(8085.4, 2889.75) * mm});
            skLineSegment(sketch, "E56.right", {"start": v(8263.2, 3042.15) * mm, "end": v(8263.2, 2889.75) * mm});
            skLineSegment(sketch, "E57.bottom", {"start": v(10326.28, 977.9) * mm, "end": v(10148.48, 977.9) * mm});
            skLineSegment(sketch, "E57.top", {"start": v(10326.28, 825.5) * mm, "end": v(10148.48, 825.5) * mm});
            skLineSegment(sketch, "E57.left", {"start": v(10148.48, 977.9) * mm, "end": v(10148.48, 825.5) * mm});
            skLineSegment(sketch, "E57.right", {"start": v(10326.28, 977.9) * mm, "end": v(10326.28, 825.5) * mm});
            skLineSegment(sketch, "E58.bottom", {"start": v(12389.35, 825.5) * mm, "end": v(12211.55, 825.5) * mm});
            skLineSegment(sketch, "E58.top", {"start": v(12389.35, 977.9) * mm, "end": v(12211.55, 977.9) * mm});
            skLineSegment(sketch, "E58.left", {"start": v(12389.35, 977.9) * mm, "end": v(12389.35, 825.5) * mm});
            skLineSegment(sketch, "E58.right", {"start": v(12211.55, 977.9) * mm, "end": v(12211.55, 825.5) * mm});
            skLineSegment(sketch, "E59", {"start": v(8263.2, 2889.75) * mm, "end": v(10148.48, 2889.75) * mm, "construction": true});
            skLineSegment(sketch, "E60", {"start": v(10326.28, 2889.75) * mm, "end": v(12211.55, 2889.75) * mm, "construction": true});
            skLineSegment(sketch, "E61", {"start": v(10148.48, 2889.75) * mm, "end": v(10326.28, 2889.75) * mm});
            skLineSegment(sketch, "E62", {"start": v(12211.55, 901.7) * mm, "end": v(12389.35, 901.7) * mm, "construction": true});
            skLineSegment(sketch, "E63", {"start": v(6200.14, 2889.75) * mm, "end": v(8085.4, 2889.75) * mm, "construction": true});
            skSolve(sketch);
        }
        {
            var Q0;
            Q0 = qSketchRegion(id + "F14", true);
            var Q1;
            Q1=makeQuery(id+"F1.opExtrude","CAP_FACE",FACE,{"disambiguationData":[OSD([sQuery(id+"F0.wireOp",EDGE,"E3.bottom"),sQuery(id+"F0.wireOp",EDGE,"E3.top"),sQuery(id+"F0.wireOp",EDGE,"E3.left"),sQuery(id+"F0.wireOp",EDGE,"E3.right")])],"isStart":true});
            extrude(context, id + "F15", {"entities" : qUnion([Q0]), "operationType" : NewBodyOperationType.ADD, "endBound" : BoundingType.UP_TO_SURFACE, "depth" : 25.4 * mm, "endBoundEntityFace" : qUnion([Q1]), "offsetDistance" : 25.4 * mm});
        }
        {
            var Q0;
            Q0=makeQuery(id+"F11.boolean.opBoolean","MERGE",FACE,{"derivedFrom":[makeQuery(id+"F9.boolean.opBoolean","MERGE",FACE,{"derivedFrom":[makeQuery(id+"F7.boolean.opBoolean","MERGE",FACE,{"derivedFrom":[makeQuery(id+"F5.boolean.opBoolean","MERGE",FACE,{"derivedFrom":[makeQuery(id+"F3.opExtrude","CAP_FACE",FACE,{"disambiguationData":[OSD([sQuery(id+"F2.wireOp",EDGE,"E8.0"),sQuery(id+"F2.wireOp",EDGE,"E9.0"),sQuery(id+"F2.wireOp",EDGE,"E9.1"),sQuery(id+"F2.wireOp",EDGE,"E10"),sQuery(id+"F2.wireOp",EDGE,"E11"),sQuery(id+"F2.wireOp",EDGE,"E12"),sQuery(id+"F2.wireOp",EDGE,"E14.0"),sQuery(id+"F2.wireOp",EDGE,"E14.1"),sQuery(id+"F2.wireOp",EDGE,"E14.2"),sQuery(id+"F2.wireOp",EDGE,"E14.3"),sQuery(id+"F2.wireOp",EDGE,"E14.4"),sQuery(id+"F2.wireOp",EDGE,"E14.5")])],"isStart":false}),makeQuery(id+"F5.opExtrude","CAP_FACE",FACE,{"disambiguationData":[OSD([sQuery(id+"F4.wireOp",EDGE,"E15.bottom"),sQuery(id+"F4.wireOp",EDGE,"E15.top"),sQuery(id+"F4.wireOp",EDGE,"E15.left"),sQuery(id+"F4.wireOp",EDGE,"E15.right")])],"isStart":false})]}),makeQuery(id+"F7.opExtrude","CAP_FACE",FACE,{"disambiguationData":[OSD([sQuery(id+"F6.wireOp",EDGE,"E16.bottom"),sQuery(id+"F6.wireOp",EDGE,"E16.top"),sQuery(id+"F6.wireOp",EDGE,"E16.left"),sQuery(id+"F6.wireOp",EDGE,"E16.right")])],"isStart":false}),makeQuery(id+"F7.opExtrude","CAP_FACE",FACE,{"disambiguationData":[OSD([sQuery(id+"F6.wireOp",EDGE,"E17.1.0.0"),sQuery(id+"F6.wireOp",EDGE,"E17.1.0.1"),sQuery(id+"F6.wireOp",EDGE,"E17.1.0.2"),sQuery(id+"F6.wireOp",EDGE,"E17.1.0.3")])],"isStart":false}),makeQuery(id+"F7.opExtrude","CAP_FACE",FACE,{"disambiguationData":[OSD([sQuery(id+"F6.wireOp",EDGE,"E17.2.0.0"),sQuery(id+"F6.wireOp",EDGE,"E17.2.0.1"),sQuery(id+"F6.wireOp",EDGE,"E17.2.0.2"),sQuery(id+"F6.wireOp",EDGE,"E17.2.0.3")])],"isStart":false}),makeQuery(id+"F7.opExtrude","CAP_FACE",FACE,{"disambiguationData":[OSD([sQuery(id+"F6.wireOp",EDGE,"E17.3.0.0"),sQuery(id+"F6.wireOp",EDGE,"E17.3.0.1"),sQuery(id+"F6.wireOp",EDGE,"E17.3.0.2"),sQuery(id+"F6.wireOp",EDGE,"E17.3.0.3")])],"isStart":false}),makeQuery(id+"F7.opExtrude","CAP_FACE",FACE,{"disambiguationData":[OSD([sQuery(id+"F6.wireOp",EDGE,"E17.4.0.0"),sQuery(id+"F6.wireOp",EDGE,"E17.4.0.1"),sQuery(id+"F6.wireOp",EDGE,"E17.4.0.2"),sQuery(id+"F6.wireOp",EDGE,"E17.4.0.3")])],"isStart":false}),makeQuery(id+"F7.opExtrude","CAP_FACE",FACE,{"disambiguationData":[OSD([sQuery(id+"F6.wireOp",EDGE,"E17.5.0.0"),sQuery(id+"F6.wireOp",EDGE,"E17.5.0.1"),sQuery(id+"F6.wireOp",EDGE,"E17.5.0.2"),sQuery(id+"F6.wireOp",EDGE,"E17.5.0.3")])],"isStart":false}),makeQuery(id+"F7.opExtrude","CAP_FACE",FACE,{"disambiguationData":[OSD([sQuery(id+"F6.wireOp",EDGE,"E17.6.0.0"),sQuery(id+"F6.wireOp",EDGE,"E17.6.0.1"),sQuery(id+"F6.wireOp",EDGE,"E17.6.0.2"),sQuery(id+"F6.wireOp",EDGE,"E17.6.0.3")])],"isStart":false}),makeQuery(id+"F7.opExtrude","CAP_FACE",FACE,{"disambiguationData":[OSD([sQuery(id+"F6.wireOp",EDGE,"E17.7.0.0"),sQuery(id+"F6.wireOp",EDGE,"E17.7.0.1"),sQuery(id+"F6.wireOp",EDGE,"E17.7.0.2"),sQuery(id+"F6.wireOp",EDGE,"E17.7.0.3")])],"isStart":false}),makeQuery(id+"F7.opExtrude","CAP_FACE",FACE,{"disambiguationData":[OSD([sQuery(id+"F6.wireOp",EDGE,"E17.8.0.0"),sQuery(id+"F6.wireOp",EDGE,"E17.8.0.1"),sQuery(id+"F6.wireOp",EDGE,"E17.8.0.2"),sQuery(id+"F6.wireOp",EDGE,"E17.8.0.3")])],"isStart":false}),makeQuery(id+"F7.opExtrude","CAP_FACE",FACE,{"disambiguationData":[OSD([sQuery(id+"F6.wireOp",EDGE,"E17.9.0.0"),sQuery(id+"F6.wireOp",EDGE,"E17.9.0.1"),sQuery(id+"F6.wireOp",EDGE,"E17.9.0.2"),sQuery(id+"F6.wireOp",EDGE,"E17.9.0.3")])],"isStart":false}),makeQuery(id+"F7.opExtrude","CAP_FACE",FACE,{"disambiguationData":[OSD([sQuery(id+"F6.wireOp",EDGE,"E18.top"),sQuery(id+"F6.wireOp",EDGE,"E18.left"),sQuery(id+"F6.wireOp",EDGE,"E18.right"),sQuery(id+"F6.wireOp",EDGE,"E20")])],"isStart":false}),makeQuery(id+"F7.opExtrude","CAP_FACE",FACE,{"disambiguationData":[OSD([sQuery(id+"F6.wireOp",EDGE,"E19.top"),sQuery(id+"F6.wireOp",EDGE,"E19.left"),sQuery(id+"F6.wireOp",EDGE,"E19.right"),sQuery(id+"F6.wireOp",EDGE,"E21.trimOffspring")])],"isStart":false})]}),makeQuery(id+"F9.opExtrude","CAP_FACE",FACE,{"disambiguationData":[OSD([sQuery(id+"F8.wireOp",EDGE,"E22"),sQuery(id+"F8.wireOp",EDGE,"E23"),sQuery(id+"F8.wireOp",EDGE,"E24"),sQuery(id+"F8.wireOp",EDGE,"E25"),sQuery(id+"F8.wireOp",EDGE,"E26"),sQuery(id+"F8.wireOp",EDGE,"E27"),sQuery(id+"F8.wireOp",EDGE,"E28")])],"isStart":true})]}),makeQuery(id+"F11.opExtrude","CAP_FACE",FACE,{"disambiguationData":[OSD([sQuery(id+"F10.wireOp",EDGE,"E29.bottom"),sQuery(id+"F10.wireOp",EDGE,"E29.top"),sQuery(id+"F10.wireOp",EDGE,"E29.left"),sQuery(id+"F10.wireOp",EDGE,"E29.right")])],"isStart":true})]});
            var sketch = newSketch(context, id + "F16", { "sketchPlane" : qUnion([Q0])});
            skLineSegment(sketch, "E64.bottom", {"start": v(5245.1, -4020.05) * mm, "end": v(6045.2, -4020.05) * mm});
            skLineSegment(sketch, "E64.top", {"start": v(5245.1, -2019.3) * mm, "end": v(6045.2, -2019.3) * mm});
            skLineSegment(sketch, "E64.left", {"start": v(5245.1, -4020.05) * mm, "end": v(5245.1, -2019.3) * mm});
            skLineSegment(sketch, "E64.right", {"start": v(6045.2, -4020.05) * mm, "end": v(6045.2, -2019.3) * mm});
            skLineSegment(sketch, "E65.bottom", {"start": v(12313.15, -2965.95) * mm, "end": v(8058.65, -2965.95) * mm});
            skLineSegment(sketch, "E65.top", {"start": v(12313.15, 1200.65) * mm, "end": v(8058.65, 1200.65) * mm});
            skLineSegment(sketch, "E65.left", {"start": v(12313.15, -2965.95) * mm, "end": v(12313.15, 1200.65) * mm});
            skLineSegment(sketch, "E65.right", {"start": v(8058.65, -2965.95) * mm, "end": v(8058.65, 1200.65) * mm});
            skLineSegment(sketch, "E66.bottom", {"start": v(7086.6, -2019.3) * mm, "end": v(6121.4, -2019.3) * mm});
            skLineSegment(sketch, "E66.top", {"start": v(6121.4, -2965.95) * mm, "end": v(7086.6, -2965.95) * mm});
            skLineSegment(sketch, "E66.left", {"start": v(6121.4, -2019.3) * mm, "end": v(6121.4, -2965.95) * mm});
            skLineSegment(sketch, "E66.right", {"start": v(7086.6, -2019.3) * mm, "end": v(7086.6, -2965.95) * mm});
            skLineSegment(sketch, "E67", {"start": v(7124.7, -2965.95) * mm, "end": v(8020.55, -2965.95) * mm});
            skLineSegment(sketch, "E68", {"start": v(8020.55, -2965.95) * mm, "end": v(8020.55, -1101.13) * mm});
            skLineSegment(sketch, "E69", {"start": v(8020.55, -1101.13) * mm, "end": v(7124.7, -1996.98) * mm});
            skLineSegment(sketch, "E70", {"start": v(7124.7, -1996.98) * mm, "end": v(7124.7, -2965.95) * mm});
            skSolve(sketch);
        }
        {
            var Q0;
            Q0 = qSketchRegion(id + "F16", true);
            var Q1;
            Q1=makeQuery(id+"F11.boolean.opBoolean","MERGE",FACE,{"derivedFrom":[makeQuery(id+"F9.opExtrude","CAP_FACE",FACE,{"disambiguationData":[OSD([sQuery(id+"F8.wireOp",EDGE,"E22"),sQuery(id+"F8.wireOp",EDGE,"E23"),sQuery(id+"F8.wireOp",EDGE,"E24"),sQuery(id+"F8.wireOp",EDGE,"E25"),sQuery(id+"F8.wireOp",EDGE,"E26"),sQuery(id+"F8.wireOp",EDGE,"E27"),sQuery(id+"F8.wireOp",EDGE,"E28")])],"isStart":false}),makeQuery(id+"F11.opExtrude","CAP_FACE",FACE,{"disambiguationData":[OSD([sQuery(id+"F10.wireOp",EDGE,"E29.bottom"),sQuery(id+"F10.wireOp",EDGE,"E29.top"),sQuery(id+"F10.wireOp",EDGE,"E29.left"),sQuery(id+"F10.wireOp",EDGE,"E29.right")])],"isStart":false})]});
            extrude(context, id + "F17", {"entities" : qUnion([Q0]), "operationType" : NewBodyOperationType.REMOVE, "endBound" : BoundingType.UP_TO_SURFACE, "oppositeDirection" : true, "depth" : 25.4 * mm, "endBoundEntityFace" : qUnion([Q1]), "offsetDistance" : 25.4 * mm});
        }
        {
            var Q0;
            Q0=makeQuery(id+"F11.boolean.opBoolean","MERGE",FACE,{"derivedFrom":[makeQuery(id+"F9.boolean.opBoolean","MERGE",FACE,{"derivedFrom":[makeQuery(id+"F7.boolean.opBoolean","MERGE",FACE,{"derivedFrom":[makeQuery(id+"F5.boolean.opBoolean","MERGE",FACE,{"derivedFrom":[makeQuery(id+"F3.opExtrude","CAP_FACE",FACE,{"disambiguationData":[OSD([sQuery(id+"F2.wireOp",EDGE,"E8.0"),sQuery(id+"F2.wireOp",EDGE,"E9.0"),sQuery(id+"F2.wireOp",EDGE,"E9.1"),sQuery(id+"F2.wireOp",EDGE,"E10"),sQuery(id+"F2.wireOp",EDGE,"E11"),sQuery(id+"F2.wireOp",EDGE,"E12"),sQuery(id+"F2.wireOp",EDGE,"E14.0"),sQuery(id+"F2.wireOp",EDGE,"E14.1"),sQuery(id+"F2.wireOp",EDGE,"E14.2"),sQuery(id+"F2.wireOp",EDGE,"E14.3"),sQuery(id+"F2.wireOp",EDGE,"E14.4"),sQuery(id+"F2.wireOp",EDGE,"E14.5")])],"isStart":false}),makeQuery(id+"F5.opExtrude","CAP_FACE",FACE,{"disambiguationData":[OSD([sQuery(id+"F4.wireOp",EDGE,"E15.bottom"),sQuery(id+"F4.wireOp",EDGE,"E15.top"),sQuery(id+"F4.wireOp",EDGE,"E15.left"),sQuery(id+"F4.wireOp",EDGE,"E15.right")])],"isStart":false})]}),makeQuery(id+"F7.opExtrude","CAP_FACE",FACE,{"disambiguationData":[OSD([sQuery(id+"F6.wireOp",EDGE,"E16.bottom"),sQuery(id+"F6.wireOp",EDGE,"E16.top"),sQuery(id+"F6.wireOp",EDGE,"E16.left"),sQuery(id+"F6.wireOp",EDGE,"E16.right")])],"isStart":false}),makeQuery(id+"F7.opExtrude","CAP_FACE",FACE,{"disambiguationData":[OSD([sQuery(id+"F6.wireOp",EDGE,"E17.1.0.0"),sQuery(id+"F6.wireOp",EDGE,"E17.1.0.1"),sQuery(id+"F6.wireOp",EDGE,"E17.1.0.2"),sQuery(id+"F6.wireOp",EDGE,"E17.1.0.3")])],"isStart":false}),makeQuery(id+"F7.opExtrude","CAP_FACE",FACE,{"disambiguationData":[OSD([sQuery(id+"F6.wireOp",EDGE,"E17.2.0.0"),sQuery(id+"F6.wireOp",EDGE,"E17.2.0.1"),sQuery(id+"F6.wireOp",EDGE,"E17.2.0.2"),sQuery(id+"F6.wireOp",EDGE,"E17.2.0.3")])],"isStart":false}),makeQuery(id+"F7.opExtrude","CAP_FACE",FACE,{"disambiguationData":[OSD([sQuery(id+"F6.wireOp",EDGE,"E17.3.0.0"),sQuery(id+"F6.wireOp",EDGE,"E17.3.0.1"),sQuery(id+"F6.wireOp",EDGE,"E17.3.0.2"),sQuery(id+"F6.wireOp",EDGE,"E17.3.0.3")])],"isStart":false}),makeQuery(id+"F7.opExtrude","CAP_FACE",FACE,{"disambiguationData":[OSD([sQuery(id+"F6.wireOp",EDGE,"E17.4.0.0"),sQuery(id+"F6.wireOp",EDGE,"E17.4.0.1"),sQuery(id+"F6.wireOp",EDGE,"E17.4.0.2"),sQuery(id+"F6.wireOp",EDGE,"E17.4.0.3")])],"isStart":false}),makeQuery(id+"F7.opExtrude","CAP_FACE",FACE,{"disambiguationData":[OSD([sQuery(id+"F6.wireOp",EDGE,"E17.5.0.0"),sQuery(id+"F6.wireOp",EDGE,"E17.5.0.1"),sQuery(id+"F6.wireOp",EDGE,"E17.5.0.2"),sQuery(id+"F6.wireOp",EDGE,"E17.5.0.3")])],"isStart":false}),makeQuery(id+"F7.opExtrude","CAP_FACE",FACE,{"disambiguationData":[OSD([sQuery(id+"F6.wireOp",EDGE,"E17.6.0.0"),sQuery(id+"F6.wireOp",EDGE,"E17.6.0.1"),sQuery(id+"F6.wireOp",EDGE,"E17.6.0.2"),sQuery(id+"F6.wireOp",EDGE,"E17.6.0.3")])],"isStart":false}),makeQuery(id+"F7.opExtrude","CAP_FACE",FACE,{"disambiguationData":[OSD([sQuery(id+"F6.wireOp",EDGE,"E17.7.0.0"),sQuery(id+"F6.wireOp",EDGE,"E17.7.0.1"),sQuery(id+"F6.wireOp",EDGE,"E17.7.0.2"),sQuery(id+"F6.wireOp",EDGE,"E17.7.0.3")])],"isStart":false}),makeQuery(id+"F7.opExtrude","CAP_FACE",FACE,{"disambiguationData":[OSD([sQuery(id+"F6.wireOp",EDGE,"E17.8.0.0"),sQuery(id+"F6.wireOp",EDGE,"E17.8.0.1"),sQuery(id+"F6.wireOp",EDGE,"E17.8.0.2"),sQuery(id+"F6.wireOp",EDGE,"E17.8.0.3")])],"isStart":false}),makeQuery(id+"F7.opExtrude","CAP_FACE",FACE,{"disambiguationData":[OSD([sQuery(id+"F6.wireOp",EDGE,"E17.9.0.0"),sQuery(id+"F6.wireOp",EDGE,"E17.9.0.1"),sQuery(id+"F6.wireOp",EDGE,"E17.9.0.2"),sQuery(id+"F6.wireOp",EDGE,"E17.9.0.3")])],"isStart":false}),makeQuery(id+"F7.opExtrude","CAP_FACE",FACE,{"disambiguationData":[OSD([sQuery(id+"F6.wireOp",EDGE,"E18.top"),sQuery(id+"F6.wireOp",EDGE,"E18.left"),sQuery(id+"F6.wireOp",EDGE,"E18.right"),sQuery(id+"F6.wireOp",EDGE,"E20")])],"isStart":false}),makeQuery(id+"F7.opExtrude","CAP_FACE",FACE,{"disambiguationData":[OSD([sQuery(id+"F6.wireOp",EDGE,"E19.top"),sQuery(id+"F6.wireOp",EDGE,"E19.left"),sQuery(id+"F6.wireOp",EDGE,"E19.right"),sQuery(id+"F6.wireOp",EDGE,"E21.trimOffspring")])],"isStart":false})]}),makeQuery(id+"F9.opExtrude","CAP_FACE",FACE,{"disambiguationData":[OSD([sQuery(id+"F8.wireOp",EDGE,"E22"),sQuery(id+"F8.wireOp",EDGE,"E23"),sQuery(id+"F8.wireOp",EDGE,"E24"),sQuery(id+"F8.wireOp",EDGE,"E25"),sQuery(id+"F8.wireOp",EDGE,"E26"),sQuery(id+"F8.wireOp",EDGE,"E27"),sQuery(id+"F8.wireOp",EDGE,"E28")])],"isStart":true})]}),makeQuery(id+"F11.opExtrude","CAP_FACE",FACE,{"disambiguationData":[OSD([sQuery(id+"F10.wireOp",EDGE,"E29.bottom"),sQuery(id+"F10.wireOp",EDGE,"E29.top"),sQuery(id+"F10.wireOp",EDGE,"E29.left"),sQuery(id+"F10.wireOp",EDGE,"E29.right")])],"isStart":true})]});
            var sketch = newSketch(context, id + "F18", { "sketchPlane" : qUnion([Q0])});
            skLineSegment(sketch, "E71.bottom", {"start": v(8223.75, 1200.65) * mm, "end": v(8261.85, 1200.65) * mm});
            skLineSegment(sketch, "E71.top", {"start": v(8223.75, -2965.95) * mm, "end": v(8261.85, -2965.95) * mm});
            skLineSegment(sketch, "E71.left", {"start": v(8223.75, 1200.65) * mm, "end": v(8223.75, -2965.95) * mm});
            skLineSegment(sketch, "E71.right", {"start": v(8261.85, 1200.65) * mm, "end": v(8261.85, -2965.95) * mm});
            skLineSegment(sketch, "E72.1.0.0", {"start": v(8630.15, -2965.95) * mm, "end": v(8668.25, -2965.95) * mm});
            skLineSegment(sketch, "E72.1.0.1", {"start": v(8668.25, 1200.65) * mm, "end": v(8668.25, -2965.95) * mm});
            skLineSegment(sketch, "E72.1.0.2", {"start": v(8630.15, 1200.65) * mm, "end": v(8668.25, 1200.65) * mm});
            skLineSegment(sketch, "E72.1.0.3", {"start": v(8630.15, 1200.65) * mm, "end": v(8630.15, -2965.95) * mm});
            skLineSegment(sketch, "E72.2.0.0", {"start": v(9036.55, -2965.95) * mm, "end": v(9074.65, -2965.95) * mm});
            skLineSegment(sketch, "E72.2.0.1", {"start": v(9074.65, 1200.65) * mm, "end": v(9074.65, -2965.95) * mm});
            skLineSegment(sketch, "E72.2.0.2", {"start": v(9036.55, 1200.65) * mm, "end": v(9074.65, 1200.65) * mm});
            skLineSegment(sketch, "E72.2.0.3", {"start": v(9036.55, 1200.65) * mm, "end": v(9036.55, -2965.95) * mm});
            skLineSegment(sketch, "E72.direction1", {"start": v(8223.75, -2965.95) * mm, "end": v(8630.15, -2965.95) * mm, "construction": true});
            skLineSegment(sketch, "E73.0.3.0", {"start": v(9442.95, -2965.95) * mm, "end": v(9481.05, -2965.95) * mm});
            skLineSegment(sketch, "E73.3.3.0", {"start": v(9481.05, 1200.65) * mm, "end": v(9481.05, -2965.95) * mm});
            skLineSegment(sketch, "E73.6.3.0", {"start": v(9442.95, 1200.65) * mm, "end": v(9481.05, 1200.65) * mm});
            skLineSegment(sketch, "E73.9.3.0", {"start": v(9442.95, 1200.65) * mm, "end": v(9442.95, -2965.95) * mm});
            skLineSegment(sketch, "E73.0.4.0", {"start": v(9849.35, -2965.95) * mm, "end": v(9887.45, -2965.95) * mm});
            skLineSegment(sketch, "E73.3.4.0", {"start": v(9887.45, 1200.65) * mm, "end": v(9887.45, -2965.95) * mm});
            skLineSegment(sketch, "E73.6.4.0", {"start": v(9849.35, 1200.65) * mm, "end": v(9887.45, 1200.65) * mm});
            skLineSegment(sketch, "E73.9.4.0", {"start": v(9849.35, 1200.65) * mm, "end": v(9849.35, -2965.95) * mm});
            skLineSegment(sketch, "E73.0.5.0", {"start": v(10255.75, -2965.95) * mm, "end": v(10293.85, -2965.95) * mm});
            skLineSegment(sketch, "E73.3.5.0", {"start": v(10293.85, 1200.65) * mm, "end": v(10293.85, -2965.95) * mm});
            skLineSegment(sketch, "E73.6.5.0", {"start": v(10255.75, 1200.65) * mm, "end": v(10293.85, 1200.65) * mm});
            skLineSegment(sketch, "E73.9.5.0", {"start": v(10255.75, 1200.65) * mm, "end": v(10255.75, -2965.95) * mm});
            skLineSegment(sketch, "E73.0.6.0", {"start": v(10662.15, -2965.95) * mm, "end": v(10700.25, -2965.95) * mm});
            skLineSegment(sketch, "E73.3.6.0", {"start": v(10700.25, 1200.65) * mm, "end": v(10700.25, -2965.95) * mm});
            skLineSegment(sketch, "E73.6.6.0", {"start": v(10662.15, 1200.65) * mm, "end": v(10700.25, 1200.65) * mm});
            skLineSegment(sketch, "E73.9.6.0", {"start": v(10662.15, 1200.65) * mm, "end": v(10662.15, -2965.95) * mm});
            skLineSegment(sketch, "E73.0.7.0", {"start": v(11068.55, -2965.95) * mm, "end": v(11106.65, -2965.95) * mm});
            skLineSegment(sketch, "E73.3.7.0", {"start": v(11106.65, 1200.65) * mm, "end": v(11106.65, -2965.95) * mm});
            skLineSegment(sketch, "E73.6.7.0", {"start": v(11068.55, 1200.65) * mm, "end": v(11106.65, 1200.65) * mm});
            skLineSegment(sketch, "E73.9.7.0", {"start": v(11068.55, 1200.65) * mm, "end": v(11068.55, -2965.95) * mm});
            skLineSegment(sketch, "E73.0.8.0", {"start": v(11474.95, -2965.95) * mm, "end": v(11513.05, -2965.95) * mm});
            skLineSegment(sketch, "E73.3.8.0", {"start": v(11513.05, 1200.65) * mm, "end": v(11513.05, -2965.95) * mm});
            skLineSegment(sketch, "E73.6.8.0", {"start": v(11474.95, 1200.65) * mm, "end": v(11513.05, 1200.65) * mm});
            skLineSegment(sketch, "E73.9.8.0", {"start": v(11474.95, 1200.65) * mm, "end": v(11474.95, -2965.95) * mm});
            skLineSegment(sketch, "E73.0.9.0", {"start": v(11881.35, -2965.95) * mm, "end": v(11919.45, -2965.95) * mm});
            skLineSegment(sketch, "E73.3.9.0", {"start": v(11919.45, 1200.65) * mm, "end": v(11919.45, -2965.95) * mm});
            skLineSegment(sketch, "E73.6.9.0", {"start": v(11881.35, 1200.65) * mm, "end": v(11919.45, 1200.65) * mm});
            skLineSegment(sketch, "E73.9.9.0", {"start": v(11881.35, 1200.65) * mm, "end": v(11881.35, -2965.95) * mm});
            skSolve(sketch);
        }
        {
            var Q0;
            Q0 = qSketchRegion(id + "F18", true);
            var Q1;
            {var subQ3=sQuery(id+"F8.wireOp",EDGE,"E28");var subQ4=sQuery(id+"F8.wireOp",EDGE,"E27");var subQ6=sQuery(id+"F8.wireOp",EDGE,"E26");var subQ7=sQuery(id+"F10.wireOp",EDGE,"E29.left");var subQ8=sQuery(id+"F10.wireOp",EDGE,"E29.top");var subQ9=sQuery(id+"F8.wireOp",EDGE,"E25");var subQ11=sQuery(id+"F10.wireOp",EDGE,"E29.right");var subQ12=sQuery(id+"F8.wireOp",EDGE,"E24");var subQ13=sQuery(id+"F8.wireOp",EDGE,"E23");var subQ14=sQuery(id+"F8.wireOp",EDGE,"E22");Q1=makeQuery(id+"F17.boolean.opBoolean","SPLIT",FACE,{"disambiguationData":[TD([makeQuery(id+"F1.opExtrude","SWEPT_FACE",FACE,{"disambiguationData":[OSD([sQuery(id+"F0.wireOp",EDGE,"E3.bottom")])]})])],"derivedFrom":makeQuery(id+"F11.boolean.opBoolean","MERGE",FACE,{"derivedFrom":[makeQuery(id+"F9.opExtrude","CAP_FACE",FACE,{"disambiguationData":[OSD([subQ14,subQ13,subQ12,subQ9,subQ6,subQ4,subQ3])],"isStart":false}),makeQuery(id+"F11.opExtrude","CAP_FACE",FACE,{"disambiguationData":[OSD([sQuery(id+"F10.wireOp",EDGE,"E29.bottom"),subQ8,subQ7,subQ11])],"isStart":false})]})});}
            extrude(context, id + "F19", {"entities" : qUnion([Q0]), "operationType" : NewBodyOperationType.ADD, "endBound" : BoundingType.UP_TO_SURFACE, "oppositeDirection" : true, "depth" : 25.4 * mm, "endBoundEntityFace" : qUnion([Q1]), "offsetDistance" : 25.4 * mm});
        }
    });
